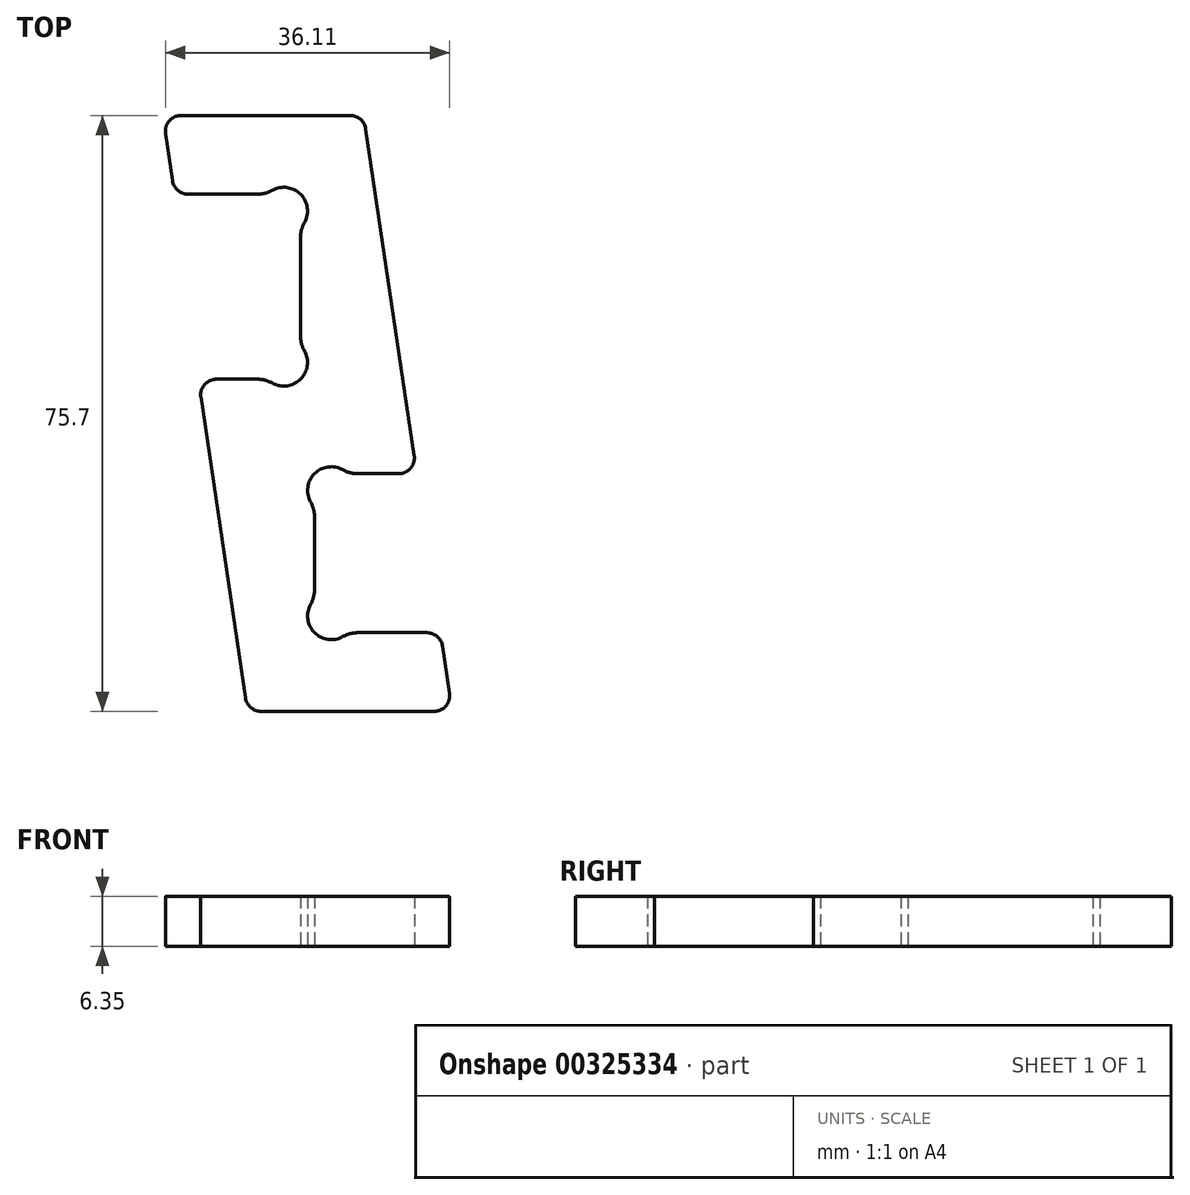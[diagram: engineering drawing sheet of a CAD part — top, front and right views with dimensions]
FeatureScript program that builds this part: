
annotation { "Feature Type Name" : "Feature", "Feature Type Description" : "" }
export const myFeature = defineFeature(function(context is Context, id is Id, definition is map)
    precondition{}
    {
        {
            var Q0;
            Q0=qCreatedBy(makeId("Top.planeOp"),FACE);
            var sketch = newSketch(context, id + "F0", { "sketchPlane" : qUnion([Q0])});
            skLineSegment(sketch, "E0", {"start": v(0, 0) * mm, "end": v(-26, 0) * mm});
            skLineSegment(sketch, "E1", {"start": v(-26, 0) * mm, "end": v(-32.27, 42.2) * mm});
            skLineSegment(sketch, "E2", {"start": v(-32.27, 42.2) * mm, "end": v(-19.27, 42.2) * mm});
            skLineSegment(sketch, "E3", {"start": v(-19.27, 42.2) * mm, "end": v(-19.27, 65.7) * mm});
            skLineSegment(sketch, "E4", {"start": v(-19.27, 65.7) * mm, "end": v(-35.27, 65.7) * mm});
            skLineSegment(sketch, "E5", {"start": v(-35.27, 65.7) * mm, "end": v(-36.75, 75.7) * mm});
            skLineSegment(sketch, "E6", {"start": v(-36.75, 75.7) * mm, "end": v(-11.24, 75.7) * mm});
            skLineSegment(sketch, "E7", {"start": v(-11.24, 75.7) * mm, "end": v(-4.49, 30.2) * mm});
            skLineSegment(sketch, "E8", {"start": v(-4.49, 30.2) * mm, "end": v(-17.49, 30.2) * mm});
            skLineSegment(sketch, "E9", {"start": v(-17.49, 30.2) * mm, "end": v(-17.49, 10) * mm});
            skLineSegment(sketch, "E10", {"start": v(-17.49, 10) * mm, "end": v(-1.49, 10) * mm});
            skLineSegment(sketch, "E11", {"start": v(-1.49, 10) * mm, "end": v(0, 0) * mm});
            skLineSegment(sketch, "E12", {"start": v(-17.49, 30.2) * mm, "end": v(-19.27, 42.2) * mm, "construction": true});
            skLineSegment(sketch, "E13", {"start": v(-19.27, 65.7) * mm, "end": v(-19.27, 75.7) * mm, "construction": true});
            skLineSegment(sketch, "E14", {"start": v(-17.49, 10) * mm, "end": v(-17.49, 0) * mm, "construction": true});
            skCircle(sketch, "E15", {"center": v(-15.36, 12.12) * mm, "radius": 3 * mm});
            skLineSegment(sketch, "E16", {"start": v(-15.36, 12.12) * mm, "end": v(-17.49, 10) * mm, "construction": true});
            skLineSegment(sketch, "E17", {"start": v(-15.36, 12.12) * mm, "end": v(-15.36, 10) * mm, "construction": true});
            skLineSegment(sketch, "E18", {"start": v(-15.36, 10) * mm, "end": v(-15.36, 12.12) * mm, "construction": true});
            skLineSegment(sketch, "E19", {"start": v(-15.36, 12.12) * mm, "end": v(-17.49, 12.12) * mm, "construction": true});
            skCircle(sketch, "E20", {"center": v(-15.36, 28.08) * mm, "radius": 3 * mm});
            skCircle(sketch, "E21", {"center": v(-21.39, 44.32) * mm, "radius": 3 * mm});
            skCircle(sketch, "E22", {"center": v(-21.39, 63.58) * mm, "radius": 3 * mm});
            skLineSegment(sketch, "E23", {"start": v(-15.36, 28.08) * mm, "end": v(-17.49, 30.2) * mm, "construction": true});
            skLineSegment(sketch, "E24", {"start": v(-21.39, 44.32) * mm, "end": v(-19.27, 42.2) * mm, "construction": true});
            skLineSegment(sketch, "E25", {"start": v(-19.27, 65.7) * mm, "end": v(-21.39, 63.58) * mm, "construction": true});
            skLineSegment(sketch, "E26", {"start": v(-17.49, 10) * mm, "end": v(-27.49, 10) * mm, "construction": true});
            skSolve(sketch);
        }
        {
            var Q0;
            Q0=makeQuery(id+"F0.imprint","IMPRINT",FACE,{"disambiguationData":[TD([[makeQuery(id+"F0.imprint","IMPRINT",EDGE,{"derivedFrom":sQuery(id+"F0.wireOp",EDGE,"E0")}),-1.0]])]});
            extrude(context, id + "F1", {"entities" : qUnion([Q0]), "depth" : 6.35 * mm});
        }
        {
            var Q0;
            Q0=makeQuery(id+"F1.opExtrude","SWEPT_EDGE",EDGE,{"disambiguationData":[OSD([sQuery(id+"F0.wireOp",EDGE,"E7"),sQuery(id+"F0.wireOp",EDGE,"E8")])]});
            var Q1;
            Q1=makeQuery(id+"F1.opExtrude","SWEPT_EDGE",EDGE,{"disambiguationData":[OSD([sQuery(id+"F0.wireOp",EDGE,"E5"),sQuery(id+"F0.wireOp",EDGE,"E6")])]});
            var Q2;
            Q2=makeQuery(id+"F1.opExtrude","SWEPT_EDGE",EDGE,{"disambiguationData":[OSD([sQuery(id+"F0.wireOp",EDGE,"E4"),sQuery(id+"F0.wireOp",EDGE,"E5")])]});
            var Q3;
            Q3=makeQuery(id+"F1.opExtrude","SWEPT_EDGE",EDGE,{"disambiguationData":[OSD([sQuery(id+"F0.wireOp",EDGE,"E4"),sQuery(id+"F0.wireOp",EDGE,"E5")])]});
            var Q4;
            Q4=makeQuery(id+"F1.opExtrude","SWEPT_EDGE",EDGE,{"disambiguationData":[OSD([sQuery(id+"F0.wireOp",EDGE,"E1"),sQuery(id+"F0.wireOp",EDGE,"E2")])]});
            var Q5;
            Q5=makeQuery(id+"F1.opExtrude","SWEPT_EDGE",EDGE,{"disambiguationData":[OSD([sQuery(id+"F0.wireOp",EDGE,"E1"),sQuery(id+"F0.wireOp",EDGE,"E2")])]});
            var Q6;
            Q6=makeQuery(id+"F1.opExtrude","SWEPT_EDGE",EDGE,{"disambiguationData":[OSD([sQuery(id+"F0.wireOp",EDGE,"E6"),sQuery(id+"F0.wireOp",EDGE,"E7")])]});
            var Q7;
            Q7=makeQuery(id+"F1.opExtrude","SWEPT_EDGE",EDGE,{"disambiguationData":[OSD([sQuery(id+"F0.wireOp",EDGE,"E7"),sQuery(id+"F0.wireOp",EDGE,"E8")])]});
            var Q8;
            Q8=makeQuery(id+"F1.opExtrude","SWEPT_EDGE",EDGE,{"disambiguationData":[OSD([sQuery(id+"F0.wireOp",EDGE,"E10"),sQuery(id+"F0.wireOp",EDGE,"E11")])]});
            var Q9;
            Q9=makeQuery(id+"F1.opExtrude","SWEPT_EDGE",EDGE,{"disambiguationData":[OSD([sQuery(id+"F0.wireOp",EDGE,"E10"),sQuery(id+"F0.wireOp",EDGE,"E11")])]});
            var Q10;
            Q10=makeQuery(id+"F1.opExtrude","SWEPT_EDGE",EDGE,{"disambiguationData":[OSD([sQuery(id+"F0.wireOp",EDGE,"E0"),sQuery(id+"F0.wireOp",EDGE,"E11")])]});
            var Q11;
            Q11=makeQuery(id+"F1.opExtrude","SWEPT_EDGE",EDGE,{"disambiguationData":[OSD([sQuery(id+"F0.wireOp",EDGE,"E0"),sQuery(id+"F0.wireOp",EDGE,"E1")])]});
            fillet(context, id + "F2", {"entities" : qUnion([Q0, Q1, Q2, Q3, Q4, Q5, Q6, Q7, Q8, Q9, Q10, Q11]), "radius" : 2 * mm, "tangentPropagation" : true, "allowEdgeOverflow" : false});
        }
        {
            var Q0;
            Q0=makeQuery(id+"F1.opExtrude","SWEPT_EDGE",EDGE,{"disambiguationData":[OSD([sQuery(id+"F0.wireOp",EDGE,"E4"),sQuery(id+"F0.wireOp",EDGE,"E22")])]});
            var Q1;
            Q1=makeQuery(id+"F1.opExtrude","SWEPT_EDGE",EDGE,{"disambiguationData":[OSD([sQuery(id+"F0.wireOp",EDGE,"E3"),sQuery(id+"F0.wireOp",EDGE,"E22")])]});
            var Q2;
            Q2=makeQuery(id+"F1.opExtrude","SWEPT_EDGE",EDGE,{"disambiguationData":[OSD([sQuery(id+"F0.wireOp",EDGE,"E3"),sQuery(id+"F0.wireOp",EDGE,"E21")])]});
            var Q3;
            Q3=makeQuery(id+"F1.opExtrude","SWEPT_EDGE",EDGE,{"disambiguationData":[OSD([sQuery(id+"F0.wireOp",EDGE,"E2"),sQuery(id+"F0.wireOp",EDGE,"E21")])]});
            var Q4;
            Q4=makeQuery(id+"F1.opExtrude","SWEPT_EDGE",EDGE,{"disambiguationData":[OSD([sQuery(id+"F0.wireOp",EDGE,"E8"),sQuery(id+"F0.wireOp",EDGE,"E20")])]});
            var Q5;
            Q5=makeQuery(id+"F1.opExtrude","SWEPT_EDGE",EDGE,{"disambiguationData":[OSD([sQuery(id+"F0.wireOp",EDGE,"E9"),sQuery(id+"F0.wireOp",EDGE,"E20")])]});
            var Q6;
            Q6=makeQuery(id+"F1.opExtrude","SWEPT_EDGE",EDGE,{"disambiguationData":[OSD([sQuery(id+"F0.wireOp",EDGE,"E9"),sQuery(id+"F0.wireOp",EDGE,"E15")])]});
            var Q7;
            Q7=makeQuery(id+"F1.opExtrude","SWEPT_EDGE",EDGE,{"disambiguationData":[OSD([sQuery(id+"F0.wireOp",EDGE,"E10"),sQuery(id+"F0.wireOp",EDGE,"E15")])]});
            fillet(context, id + "F3", {"entities" : qUnion([Q0, Q1, Q2, Q3, Q4, Q5, Q6, Q7]), "radius" : 4 * mm, "tangentPropagation" : true, "allowEdgeOverflow" : false});
        }
    });
